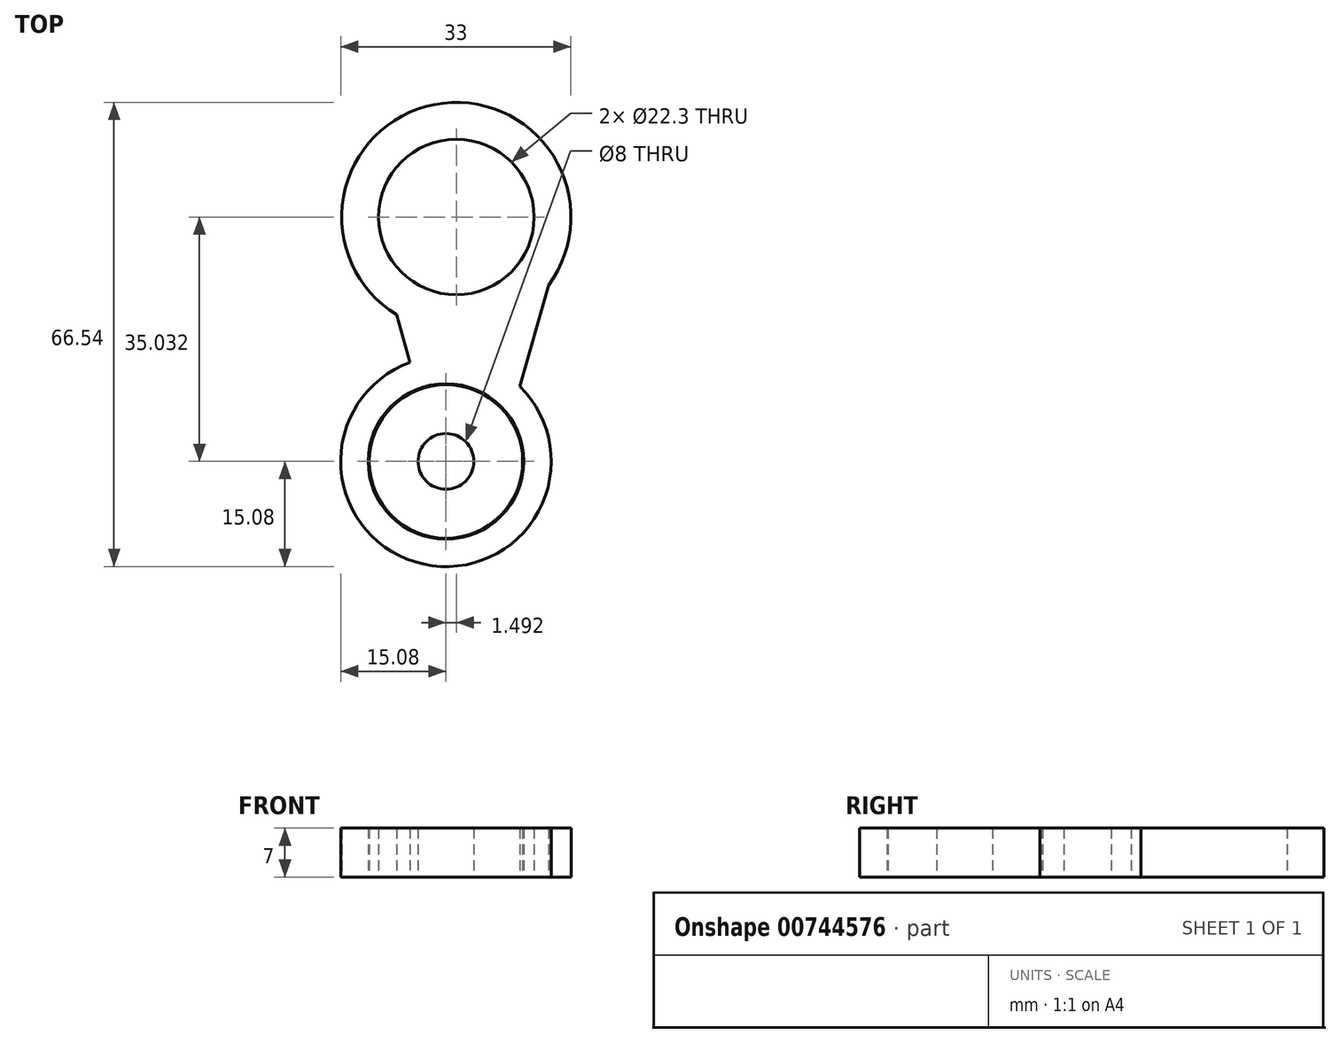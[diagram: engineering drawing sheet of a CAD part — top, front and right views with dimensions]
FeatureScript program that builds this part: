
annotation { "Feature Type Name" : "Feature", "Feature Type Description" : "" }
export const myFeature = defineFeature(function(context is Context, id is Id, definition is map)
    precondition{}
    {
        {
            var Q0;
            Q0=qCreatedBy(makeId("Top.planeOp"),FACE);
            var sketch = newSketch(context, id + "F0", { "sketchPlane" : qUnion([Q0])});
            skCircle(sketch, "E0", {"center": v(0, 0) * mm, "radius": 4 * mm});
            skCircle(sketch, "E1", {"center": v(0, 0) * mm, "radius": 11 * mm});
            skSolve(sketch);
        }
        {
            var Q0;
            Q0 = qSketchRegion(id + "F0", true);
            extrude(context, id + "F1", {"entities" : qUnion([Q0]), "depth" : 7 * mm, "offsetDistance" : 25 * mm});
        }
        {
            var Q0;
            Q0=qCreatedBy(makeId("Top.planeOp"),FACE);
            var sketch = newSketch(context, id + "F2", { "sketchPlane" : qUnion([Q0])});
            skCircle(sketch, "E2", {"center": v(0, 0) * mm, "radius": 11.15 * mm});
            skCircle(sketch, "E3", {"center": v(0, 0) * mm, "radius": 15.08 * mm});
            skSolve(sketch);
        }
        {
            var Q0;
            Q0 = qSketchRegion(id + "F2", true);
            extrude(context, id + "F3", {"entities" : qUnion([Q0]), "depth" : 7 * mm, "offsetDistance" : 25 * mm});
        }
        {
            var Q0;
            Q0=qCreatedBy(makeId("Top.planeOp"),FACE);
            var sketch = newSketch(context, id + "F4", { "sketchPlane" : qUnion([Q0])});
            skLineSegment(sketch, "E4", {"start": v(-4.84, 13.14) * mm, "end": v(-8.28, 25.26) * mm});
            skLineSegment(sketch, "E5", {"start": v(-8.28, 25.26) * mm, "end": v(14.7, 25.26) * mm});
            skLineSegment(sketch, "E6", {"start": v(14.7, 25.26) * mm, "end": v(10, 8.8) * mm});
            skLineSegment(sketch, "E7", {"start": v(10, 8.8) * mm, "end": v(6.2, 12.78) * mm});
            skLineSegment(sketch, "E8", {"start": v(6.2, 12.78) * mm, "end": v(-4.84, 13.14) * mm});
            skCircle(sketch, "E9", {"center": v(1.5, 35.03) * mm, "radius": 11.15 * mm});
            skCircle(sketch, "E10", {"center": v(1.5, 35.03) * mm, "radius": 16.43 * mm});
            skSolve(sketch);
        }
        {
            var Q0;
            Q0 = qSketchRegion(id + "F4", true);
            extrude(context, id + "F5", {"entities" : qUnion([Q0]), "operationType" : NewBodyOperationType.ADD, "depth" : 7 * mm, "offsetDistance" : 25 * mm});
        }
    });
